# Revit family: Рондо-1
name_source: partatom
category: Осветительные приборы
units: mm (PartAtom-declared; Revit-internal decimal feet)

## family parameters
Всегда вертикально = Да
Источник света = Да
На основе рабочей плоскости = Нет
Общий = Нет
При загрузке вырезать с полостями = Нет
Размер круглого соединителя = Использовать диаметр
Тип детали = Нормальный
Точка расчета площади = Нет

## types (10) — shared parameters
ADSK_URL страницы изделия = https://www.allfresco.ru
ADSK_Единица измерения = шт.
ADSK_Завод-изготовитель = ALFRESCO
ADSK_Количество фаз = 2
ADSK_Модель = Рондо-1 ДТУ-88-AF
ADSK_Напряжение = 220 В
ADSK_Полная мощность = 0 В·А
ADSK_Ток = 0 А
ADSK_Энергоэффективность = 110 лм/Вт
H_дверка = 500 мм
IP Class = IP 67
a1_фланец = 200 мм
a_фланец = 280 мм
d_верх столба = 70 мм
d_основание столба = 110 мм
d_отверстие фланец = 22 мм
h1_отступ до верхнего светильника = 70 мм
h2_расстояние между светильниками = 430 мм
h_дверь = 500 мм
h_пластина = 5 мм
h_рассеиватель = 5 мм
h_светильник = 146 мм
h_столб = 3000 мм
h_установки светильников = 1000 мм
r светильник = 445 мм
r1_дверь = 45 мм
r2_дверь = 55 мм
r_верх столба = 35 мм
r_отверстие фланец = 11 мм
r_пластина = 50 мм
r_рассеиватель = 440 мм
r_столб = 30 мм
Блок аварийного питания = Нет
Класс защиты = 1
Класс пожароопасности = F (светильники предназначены для установки непосредственно на поверхность из нормально воспламеняемых материалов)
Климатическая зона = УХЛ1
Корпус светильника = Серый металл
Материал рассеивателя = Светотехнический ПК
Область использования = Парки, скверы, общественные пространства, городская инфраструктура
Полная установленная мощность = 0 В·А
Рассеиватель = Белый_светодиод
Светофильтр = 16777215
Смещение цветовой температуры при затухании лампы = <Нет>
Таблица выбора = Таблица параметров светильников — копия
Температура эксплуатации = -40 +50
Тип ИС = LED-модуль
Тип КСС = тип Д (косинусная)
Тип ПРА = -
Тип продукции = LED-светильник
Угол наклона = 90.00°
Цветоывая температура = 2700-5500
zero-valued in all types: ADSK_Количество фаз числовое, ADSK_Коэффициент мощности

## per-type parameters (varying)
| type | 2 светильника | 3 светильника | ADSK_Артикул | ADSK_Масса | ADSK_Масса_Текст | ADSK_Наименование | ADSK_Номинальная мощность | ADSK_Размер_Высота | ADSK_Фактическая мощность | h_сужения столба | h_фланец | Артикул | Файл фотометрической сетки |
| ДТУ881 Светодиодный светильник Рондо-1 ДТУ-88-AF-ДТУП881(25Вт)-4,0 | Нет | Нет | ДТУ881 | 37 | 37 | ДТУ881 Светодиодный светильник Рондо-1 ДТУ-88-AF-ДТУП881(25Вт)-4.0 | 25 Вт | 4000 мм | 25 Вт | 2980 мм | 20 мм | 881 мм | DTU-88-AF RONDO-1 25W.ies |
| ДТУ8813 Светодиодный светильник Рондо-1 ДТУ-88-AF-ДТУП882(50Вт)-4,0 | Нет | Нет | ДТУ8813 | 37 | 37 | ДТУ8813 Светодиодный светильник Рондо-1 ДТУ-88-AF-ДТУП882(50Вт)-4.0 | 50 Вт | 4000 мм | 50 Вт | 2990 мм | 10 мм | 8813 мм | DTU-88-AF RONDO-1 50W.ies |
| ДТУ883 Светодиодный светильник Рондо-1 ДТУ-88-AF-ДТУП882(50Вт)-5,0 | Нет | Нет | ДТУ883 | 44 | 44 | ДТУ883 Светодиодный светильник Рондо-1 ДТУ-88-AF-ДТУП882(50Вт)-5.0 | 50 Вт | 5000 мм | 50 Вт | 3990 мм | 10 мм | 883 мм | DTU-88-AF RONDO-1 50W.ies |
| ДТУ885 Светодиодный светильник Рондо-1 ДТУ-88-AF-ДТУП882(50Вт)-6,0 | Нет | Нет | ДТУ885 | 53 | 53 | ДТУ885 Светодиодный светильник Рондо-1 ДТУ-88-AF-ДТУП882(50Вт)-6.0 | 50 Вт | 6000 мм | 50 Вт | 4990 мм | 10 мм | 885 мм | DTU-88-AF RONDO-1 50W.ies |
| ДТУ886 Светодиодный светильник Рондо-1 ДТУ-88-AF-ДТУП883(75Вт)-6,0 | Нет | Нет | ДТУ886 | 53 | 53 | ДТУ886 Светодиодный светильник Рондо-1 ДТУ-88-AF-ДТУП883(75Вт)-6.0 | 75 Вт | 6000 мм | 75 Вт | 4990 мм | 10 мм | 886 мм | DTU-88-AF RONDO-1 75W.ies |
| ДТУ882 Светодиодный светильник Рондо-1 ДТУ-88-AF-ДТУП881(25Вт)_ДТУП881(25Вт)(3,5)-4,0 | Да | Нет | ДТУ882 | 47 | 47 | ДТУ882 Светодиодный светильник Рондо-1 ДТУ-88-AF-ДТУП881(25Вт)_ДТУП881(25Вт)(3.5)-4.0 | 50 Вт | 4000 мм | 50 Вт | 2990 мм | 10 мм | 882 мм | DTU-88-AF RONDO-1 50W.ies |
| ДТУ884 Светодиодный светильник Рондо-1 ДТУ-88-AF-ДТУП882(50Вт)_ДТУП881(25Вт)(4,5)-5,0 | Да | Нет | ДТУ884 | 55 | 55 | ДТУ884 Светодиодный светильник Рондо-1 ДТУ-88-AF-ДТУП882(50Вт)_ДТУП881(25Вт)(4.5)-5.0 | 75 Вт | 5000 мм | 75 Вт | 3990 мм | 10 мм | 884 мм | DTU-88-AF RONDO-1 75W.ies |
| ДТУ8816 Светодиодный светильник Рондо-1 ДТУ-88-AF-ДТУП881(25Вт)_ДТУП881(25Вт)(5,5)-6,0 | Да | Нет | ДТУ8816 | 63 | 63 | ДТУ8816 Светодиодный светильник Рондо-1 ДТУ-88-AF-ДТУП881(25Вт)_ДТУП881(25Вт)(5.5)-6.0 | 50 Вт | 6000 мм | 50 Вт | 4990 мм | 10 мм | 8816 мм | DTU-88-AF RONDO-1 50W.ies |
| ДТУ887 Светодиодный светильник Рондо-1 ДТУ-88-AF-ДТУП883(75Вт)_ДТУП882(50Вт)(5,5)-6,0 | Да | Нет | ДТУ887 | 63 | 63 | ДТУ887 Светодиодный светильник Рондо-1 ДТУ-88-AF-ДТУП883(75Вт)_ДТУП882(50Вт)(5.5)-6.0 | 125 Вт | 6000 мм | 125 Вт | 4990 мм | 10 мм | 887 мм | DTU-88-AF RONDO-1 75W.ies |
| ДТУ888 Светод.светильник Рондо-1 ДТУ-88-AF-ДТУП881(25Вт)_ДТУП881(25Вт)(5,5)_ДТУП881(25Вт)(5,0)-(6,0) | Да | Да | ДТУ888 | 74 | 74 | ДТУ888 Светод.светильник Рондо-1 ДТУ-88-AF-ДТУП881(25Вт)_ДТУП881(25Вт)(5.5)_ДТУП881(25Вт)(5.0)-(6.0) | 75 Вт | 6000 мм | 75 Вт | 4990 мм | 10 мм | 888 мм | DTU-88-AF RONDO-1 75W.ies |
